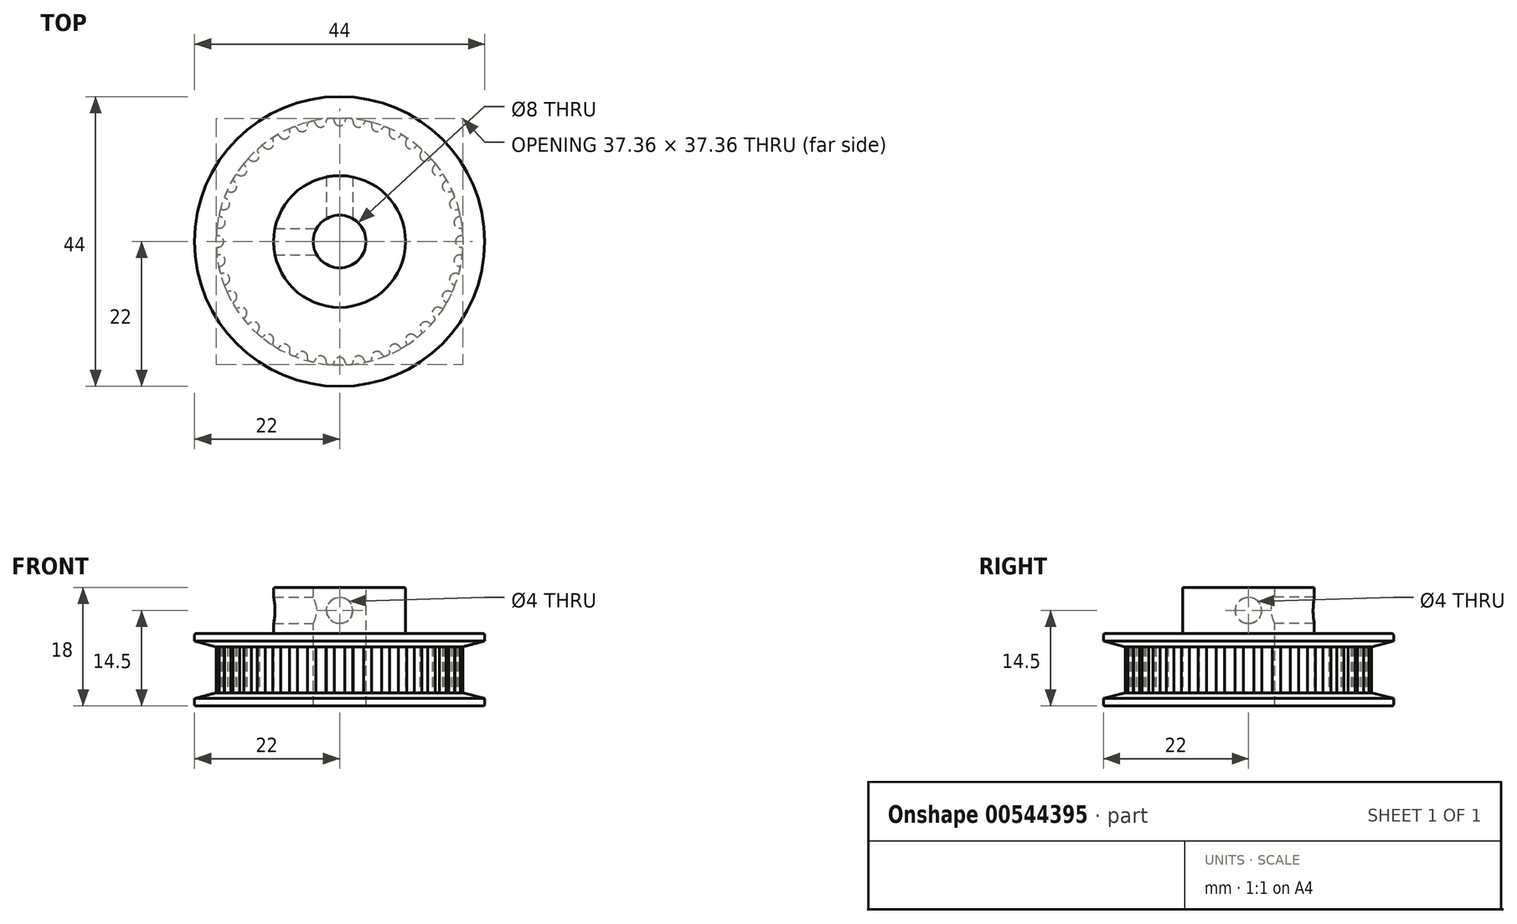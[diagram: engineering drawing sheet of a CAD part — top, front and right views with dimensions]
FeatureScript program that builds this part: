
annotation { "Feature Type Name" : "Feature", "Feature Type Description" : "" }
export const myFeature = defineFeature(function(context is Context, id is Id, definition is map)
    precondition{}
    {
        {
            assignVariable(context, id + "F0", {"name" : "teeth", "anyValue" : 40});
        }
        {
            assignVariable(context, id + "F1", {"name" : "width", "anyValue" : 7});
        }
        {
            var Q0;
            Q0=qCreatedBy(makeId("Top.planeOp"),FACE);
            var sketch = newSketch(context, id + "F2", { "sketchPlane" : qUnion([Q0])});
            skLineSegment(sketch, "E0", {"start": v(0, 0) * mm, "end": v(0, 17.58) * mm, "construction": true});
            skArc(sketch, "E1", {"start": v(1.78, 18.63) * mm, "mid": v(0.15, 18.72) * mm, "end": v(-1.47, 18.66) * mm, "construction": true});
            skArc(sketch, "E2", {"start": v(0, 17.58) * mm, "mid": v(0.49, 17.73) * mm, "end": v(0.8, 18.13) * mm});
            skLineSegment(sketch, "E3", {"start": v(0, 17.58) * mm, "end": v(0, 18.72) * mm, "construction": true});
            skLineSegment(sketch, "E4", {"start": v(0, 18.72) * mm, "end": v(0, 19.1) * mm, "construction": true});
            skArc(sketch, "E5", {"start": v(1.5, 19.04) * mm, "mid": v(0, 19.1) * mm, "end": v(-1.5, 19.04) * mm, "construction": true});
            skLineSegment(sketch, "E6", {"start": v(1.47, 18.66) * mm, "end": v(0, 0) * mm});
            skLineSegment(sketch, "E7", {"start": v(0, 0) * mm, "end": v(-1.47, 18.66) * mm});
            skArc(sketch, "E8", {"start": v(1.15, 18.68) * mm, "mid": v(0.98, 18.63) * mm, "end": v(0.9, 18.47) * mm});
            skArc(sketch, "E9", {"start": v(0.8, 18.13) * mm, "mid": v(0.85, 18.3) * mm, "end": v(0.9, 18.47) * mm});
            skArc(sketch, "E10.MirrorCS", {"start": v(0, 17.58) * mm, "mid": v(-0.49, 17.73) * mm, "end": v(-0.8, 18.13) * mm});
            skArc(sketch, "E11.MirrorCS", {"start": v(-0.8, 18.13) * mm, "mid": v(-0.85, 18.3) * mm, "end": v(-0.9, 18.47) * mm});
            skArc(sketch, "E12.MirrorCS", {"start": v(-1.15, 18.68) * mm, "mid": v(-0.98, 18.63) * mm, "end": v(-0.9, 18.47) * mm});
            skArc(sketch, "E13", {"start": v(0, 18.72) * mm, "mid": v(-0.3, 18.72) * mm, "end": v(-0.6, 18.7) * mm, "construction": true});
            skArc(sketch, "E14", {"start": v(1.39, 17.52) * mm, "mid": v(0, 17.58) * mm, "end": v(-1.39, 17.52) * mm, "construction": true});
            skArc(sketch, "E15", {"start": v(-1.15, 18.68) * mm, "mid": v(-1.31, 18.67) * mm, "end": v(-1.47, 18.66) * mm});
            skArc(sketch, "E16", {"start": v(1.15, 18.68) * mm, "mid": v(1.31, 18.67) * mm, "end": v(1.47, 18.66) * mm});
            skSolve(sketch);
        }
        {
            var Q0;
            Q0=makeQuery(id+"F2.imprint","IMPRINT",FACE,{"disambiguationData":[TD([[makeQuery(id+"F2.imprint","IMPRINT",EDGE,{"derivedFrom":sQuery(id+"F2.wireOp",EDGE,"E2")}),-1.0]])]});
            var Q1;
            {var subQ1=sQuery(id+"F2.wireOp",EDGE,"N9a9pOVT-NxnP-9PMo-Yz0L-ytRW1WlfzG62");Q1=makeQuery(id+"F2.imprint","IMPRINT",FACE,{"disambiguationData":[TD([[makeQuery(id+"F2.imprint","IMPRINT",EDGE,{"derivedFrom":subQ1}),-1.0]])]});}
            var Q2;
            {var subQ0=sQuery(id+"F2.wireOp",EDGE,"E6");Q2=makeQuery(id+"F2.imprint","IMPRINT",FACE,{"disambiguationData":[TD([[makeQuery(id+"F2.imprint","IMPRINT",EDGE,{"derivedFrom":subQ0}),-1.0]])]});}
            extrude(context, id + "F3", {"entities" : qUnion([Q0, Q1, Q2]), "depth" : (getVariable(context, 'width')) * mm, "offsetDistance" : 25 * mm, "symmetric" : true});
        }
        {
            var Q0;
            Q0=makeQuery(id+"F3.opExtrude","SWEPT_BODY",BODY,{"disambiguationData":[OSD([sQuery(id+"F2.wireOp",EDGE,"E1"),sQuery(id+"F2.wireOp",EDGE,"E2"),sQuery(id+"F2.wireOp",EDGE,"WtW3y5By-gfdo-wMA2-XeKf-OYMCoWhlFWBV"),sQuery(id+"F2.wireOp",EDGE,"E6"),sQuery(id+"F2.wireOp",EDGE,"E7"),sQuery(id+"F2.wireOp",EDGE,"N9a9pOVT-NxnP-9PMo-Yz0L-ytRW1WlfzG62"),sQuery(id+"F2.wireOp",EDGE,"E8"),sQuery(id+"F2.wireOp",EDGE,"E9"),sQuery(id+"F2.wireOp",EDGE,"E10.MirrorCS"),sQuery(id+"F2.wireOp",EDGE,"E11.MirrorCS"),sQuery(id+"F2.wireOp",EDGE,"E12.MirrorCS")])]});
            var Q1;
            Q1=makeQuery(id+"F3.opExtrude","SWEPT_EDGE",EDGE,{"disambiguationData":[OSD([sQuery(id+"F2.wireOp",EDGE,"E6"),sQuery(id+"F2.wireOp",EDGE,"E7")])]});
            circularPattern(context, id + "F4", {"operationType" : NewBodyOperationType.ADD, "entities" : qUnion([Q0]), "axis" : qUnion([Q1]), "angle" : 360 * degree, "instanceCount" : getVariable(context, 'teeth'), "equalSpace" : true});
        }
        {
            var Q0;
            {var subQ0=makeQuery(id+"F3.opExtrude","CAP_FACE",FACE,{"disambiguationData":[OSD([sQuery(id+"F2.wireOp",EDGE,"E2"),sQuery(id+"F2.wireOp",EDGE,"E6"),sQuery(id+"F2.wireOp",EDGE,"E7"),sQuery(id+"F2.wireOp",EDGE,"E8"),sQuery(id+"F2.wireOp",EDGE,"E9"),sQuery(id+"F2.wireOp",EDGE,"E10.MirrorCS"),sQuery(id+"F2.wireOp",EDGE,"E11.MirrorCS"),sQuery(id+"F2.wireOp",EDGE,"E12.MirrorCS"),sQuery(id+"F2.wireOp",EDGE,"E15"),sQuery(id+"F2.wireOp",EDGE,"E16")])],"isStart":true});Q0=makeQuery(id+"F4.boolean.opBoolean","MERGE",FACE,{"derivedFrom":[subQ0,makeQuery(id+"F4.opPattern","COPY",FACE,{"derivedFrom":subQ0,"instanceName":"1"}),makeQuery(id+"F4.opPattern","COPY",FACE,{"derivedFrom":subQ0,"instanceName":"2"}),makeQuery(id+"F4.opPattern","COPY",FACE,{"derivedFrom":subQ0,"instanceName":"3"}),makeQuery(id+"F4.opPattern","COPY",FACE,{"derivedFrom":subQ0,"instanceName":"4"}),makeQuery(id+"F4.opPattern","COPY",FACE,{"derivedFrom":subQ0,"instanceName":"5"}),makeQuery(id+"F4.opPattern","COPY",FACE,{"derivedFrom":subQ0,"instanceName":"6"}),makeQuery(id+"F4.opPattern","COPY",FACE,{"derivedFrom":subQ0,"instanceName":"7"}),makeQuery(id+"F4.opPattern","COPY",FACE,{"derivedFrom":subQ0,"instanceName":"8"}),makeQuery(id+"F4.opPattern","COPY",FACE,{"derivedFrom":subQ0,"instanceName":"9"}),makeQuery(id+"F4.opPattern","COPY",FACE,{"derivedFrom":subQ0,"instanceName":"10"}),makeQuery(id+"F4.opPattern","COPY",FACE,{"derivedFrom":subQ0,"instanceName":"11"}),makeQuery(id+"F4.opPattern","COPY",FACE,{"derivedFrom":subQ0,"instanceName":"12"}),makeQuery(id+"F4.opPattern","COPY",FACE,{"derivedFrom":subQ0,"instanceName":"13"}),makeQuery(id+"F4.opPattern","COPY",FACE,{"derivedFrom":subQ0,"instanceName":"14"}),makeQuery(id+"F4.opPattern","COPY",FACE,{"derivedFrom":subQ0,"instanceName":"15"}),makeQuery(id+"F4.opPattern","COPY",FACE,{"derivedFrom":subQ0,"instanceName":"16"}),makeQuery(id+"F4.opPattern","COPY",FACE,{"derivedFrom":subQ0,"instanceName":"17"}),makeQuery(id+"F4.opPattern","COPY",FACE,{"derivedFrom":subQ0,"instanceName":"18"}),makeQuery(id+"F4.opPattern","COPY",FACE,{"derivedFrom":subQ0,"instanceName":"19"}),makeQuery(id+"F4.opPattern","COPY",FACE,{"derivedFrom":subQ0,"instanceName":"20"}),makeQuery(id+"F4.opPattern","COPY",FACE,{"derivedFrom":subQ0,"instanceName":"21"}),makeQuery(id+"F4.opPattern","COPY",FACE,{"derivedFrom":subQ0,"instanceName":"22"}),makeQuery(id+"F4.opPattern","COPY",FACE,{"derivedFrom":subQ0,"instanceName":"23"}),makeQuery(id+"F4.opPattern","COPY",FACE,{"derivedFrom":subQ0,"instanceName":"24"}),makeQuery(id+"F4.opPattern","COPY",FACE,{"derivedFrom":subQ0,"instanceName":"25"}),makeQuery(id+"F4.opPattern","COPY",FACE,{"derivedFrom":subQ0,"instanceName":"26"}),makeQuery(id+"F4.opPattern","COPY",FACE,{"derivedFrom":subQ0,"instanceName":"27"}),makeQuery(id+"F4.opPattern","COPY",FACE,{"derivedFrom":subQ0,"instanceName":"28"}),makeQuery(id+"F4.opPattern","COPY",FACE,{"derivedFrom":subQ0,"instanceName":"29"}),makeQuery(id+"F4.opPattern","COPY",FACE,{"derivedFrom":subQ0,"instanceName":"30"}),makeQuery(id+"F4.opPattern","COPY",FACE,{"derivedFrom":subQ0,"instanceName":"31"}),makeQuery(id+"F4.opPattern","COPY",FACE,{"derivedFrom":subQ0,"instanceName":"32"}),makeQuery(id+"F4.opPattern","COPY",FACE,{"derivedFrom":subQ0,"instanceName":"33"}),makeQuery(id+"F4.opPattern","COPY",FACE,{"derivedFrom":subQ0,"instanceName":"34"}),makeQuery(id+"F4.opPattern","COPY",FACE,{"derivedFrom":subQ0,"instanceName":"35"}),makeQuery(id+"F4.opPattern","COPY",FACE,{"derivedFrom":subQ0,"instanceName":"36"}),makeQuery(id+"F4.opPattern","COPY",FACE,{"derivedFrom":subQ0,"instanceName":"37"}),makeQuery(id+"F4.opPattern","COPY",FACE,{"derivedFrom":subQ0,"instanceName":"38"}),makeQuery(id+"F4.opPattern","COPY",FACE,{"derivedFrom":subQ0,"instanceName":"39"})]});}
            var sketch = newSketch(context, id + "F5", { "sketchPlane" : qUnion([Q0])});
            skCircle(sketch, "E17", {"center": v(0, 0) * mm, "radius": 22 * mm});
            skSolve(sketch);
        }
        {
            var Q0;
            Q0=qSketchRegion(id+"F5",true);
            extrude(context, id + "F6", {"entities" : qUnion([Q0]), "operationType" : NewBodyOperationType.ADD, "depth" : 2 * mm, "offsetDistance" : 25 * mm});
        }
        {
            var Q0;
            {var subQ0=makeQuery(id+"F3.opExtrude","CAP_FACE",FACE,{"disambiguationData":[OSD([sQuery(id+"F2.wireOp",EDGE,"E2"),sQuery(id+"F2.wireOp",EDGE,"E6"),sQuery(id+"F2.wireOp",EDGE,"E7"),sQuery(id+"F2.wireOp",EDGE,"E8"),sQuery(id+"F2.wireOp",EDGE,"E9"),sQuery(id+"F2.wireOp",EDGE,"E10.MirrorCS"),sQuery(id+"F2.wireOp",EDGE,"E11.MirrorCS"),sQuery(id+"F2.wireOp",EDGE,"E12.MirrorCS"),sQuery(id+"F2.wireOp",EDGE,"E15"),sQuery(id+"F2.wireOp",EDGE,"E16")])],"isStart":false});Q0=makeQuery(id+"F4.boolean.opBoolean","MERGE",FACE,{"derivedFrom":[subQ0,makeQuery(id+"F4.opPattern","COPY",FACE,{"derivedFrom":subQ0,"instanceName":"1"}),makeQuery(id+"F4.opPattern","COPY",FACE,{"derivedFrom":subQ0,"instanceName":"2"}),makeQuery(id+"F4.opPattern","COPY",FACE,{"derivedFrom":subQ0,"instanceName":"3"}),makeQuery(id+"F4.opPattern","COPY",FACE,{"derivedFrom":subQ0,"instanceName":"4"}),makeQuery(id+"F4.opPattern","COPY",FACE,{"derivedFrom":subQ0,"instanceName":"5"}),makeQuery(id+"F4.opPattern","COPY",FACE,{"derivedFrom":subQ0,"instanceName":"6"}),makeQuery(id+"F4.opPattern","COPY",FACE,{"derivedFrom":subQ0,"instanceName":"7"}),makeQuery(id+"F4.opPattern","COPY",FACE,{"derivedFrom":subQ0,"instanceName":"8"}),makeQuery(id+"F4.opPattern","COPY",FACE,{"derivedFrom":subQ0,"instanceName":"9"}),makeQuery(id+"F4.opPattern","COPY",FACE,{"derivedFrom":subQ0,"instanceName":"10"}),makeQuery(id+"F4.opPattern","COPY",FACE,{"derivedFrom":subQ0,"instanceName":"11"}),makeQuery(id+"F4.opPattern","COPY",FACE,{"derivedFrom":subQ0,"instanceName":"12"}),makeQuery(id+"F4.opPattern","COPY",FACE,{"derivedFrom":subQ0,"instanceName":"13"}),makeQuery(id+"F4.opPattern","COPY",FACE,{"derivedFrom":subQ0,"instanceName":"14"}),makeQuery(id+"F4.opPattern","COPY",FACE,{"derivedFrom":subQ0,"instanceName":"15"}),makeQuery(id+"F4.opPattern","COPY",FACE,{"derivedFrom":subQ0,"instanceName":"16"}),makeQuery(id+"F4.opPattern","COPY",FACE,{"derivedFrom":subQ0,"instanceName":"17"}),makeQuery(id+"F4.opPattern","COPY",FACE,{"derivedFrom":subQ0,"instanceName":"18"}),makeQuery(id+"F4.opPattern","COPY",FACE,{"derivedFrom":subQ0,"instanceName":"19"}),makeQuery(id+"F4.opPattern","COPY",FACE,{"derivedFrom":subQ0,"instanceName":"20"}),makeQuery(id+"F4.opPattern","COPY",FACE,{"derivedFrom":subQ0,"instanceName":"21"}),makeQuery(id+"F4.opPattern","COPY",FACE,{"derivedFrom":subQ0,"instanceName":"22"}),makeQuery(id+"F4.opPattern","COPY",FACE,{"derivedFrom":subQ0,"instanceName":"23"}),makeQuery(id+"F4.opPattern","COPY",FACE,{"derivedFrom":subQ0,"instanceName":"24"}),makeQuery(id+"F4.opPattern","COPY",FACE,{"derivedFrom":subQ0,"instanceName":"25"}),makeQuery(id+"F4.opPattern","COPY",FACE,{"derivedFrom":subQ0,"instanceName":"26"}),makeQuery(id+"F4.opPattern","COPY",FACE,{"derivedFrom":subQ0,"instanceName":"27"}),makeQuery(id+"F4.opPattern","COPY",FACE,{"derivedFrom":subQ0,"instanceName":"28"}),makeQuery(id+"F4.opPattern","COPY",FACE,{"derivedFrom":subQ0,"instanceName":"29"}),makeQuery(id+"F4.opPattern","COPY",FACE,{"derivedFrom":subQ0,"instanceName":"30"}),makeQuery(id+"F4.opPattern","COPY",FACE,{"derivedFrom":subQ0,"instanceName":"31"}),makeQuery(id+"F4.opPattern","COPY",FACE,{"derivedFrom":subQ0,"instanceName":"32"}),makeQuery(id+"F4.opPattern","COPY",FACE,{"derivedFrom":subQ0,"instanceName":"33"}),makeQuery(id+"F4.opPattern","COPY",FACE,{"derivedFrom":subQ0,"instanceName":"34"}),makeQuery(id+"F4.opPattern","COPY",FACE,{"derivedFrom":subQ0,"instanceName":"35"}),makeQuery(id+"F4.opPattern","COPY",FACE,{"derivedFrom":subQ0,"instanceName":"36"}),makeQuery(id+"F4.opPattern","COPY",FACE,{"derivedFrom":subQ0,"instanceName":"37"}),makeQuery(id+"F4.opPattern","COPY",FACE,{"derivedFrom":subQ0,"instanceName":"38"}),makeQuery(id+"F4.opPattern","COPY",FACE,{"derivedFrom":subQ0,"instanceName":"39"})]});}
            var sketch = newSketch(context, id + "F7", { "sketchPlane" : qUnion([Q0])});
            skCircle(sketch, "E18", {"center": v(0, 0) * mm, "radius": 22 * mm});
            skSolve(sketch);
        }
        {
            var Q0;
            Q0=qSketchRegion(id+"F7",true);
            extrude(context, id + "F8", {"entities" : qUnion([Q0]), "operationType" : NewBodyOperationType.ADD, "depth" : 2 * mm, "offsetDistance" : 25 * mm});
        }
        {
            var Q0;
            Q0=makeQuery(id+"F8.opExtrude","CAP_FACE",FACE,{"disambiguationData":[OSD([sQuery(id+"F7.wireOp",EDGE,"E18")])],"isStart":false});
            var sketch = newSketch(context, id + "F9", { "sketchPlane" : qUnion([Q0])});
            skCircle(sketch, "E19", {"center": v(0, 0) * mm, "radius": 10 * mm});
            skSolve(sketch);
        }
        {
            var Q0;
            Q0=qSketchRegion(id+"F9",true);
            extrude(context, id + "F10", {"entities" : qUnion([Q0]), "operationType" : NewBodyOperationType.ADD, "depth" : 7 * mm, "offsetDistance" : 25 * mm});
        }
        {
            var Q0;
            Q0=makeQuery(id+"F10.opExtrude","CAP_FACE",FACE,{"disambiguationData":[OSD([sQuery(id+"F9.wireOp",EDGE,"E19")])],"isStart":false});
            var sketch = newSketch(context, id + "F11", { "sketchPlane" : qUnion([Q0])});
            skCircle(sketch, "E20", {"center": v(0, 0) * mm, "radius": 4 * mm});
            skSolve(sketch);
        }
        {
            var Q0;
            Q0=qSketchRegion(id+"F11",true);
            extrude(context, id + "F12", {"entities" : qUnion([Q0]), "operationType" : NewBodyOperationType.REMOVE, "endBound" : BoundingType.THROUGH_ALL, "oppositeDirection" : true, "depth" : 25 * mm, "offsetDistance" : 25 * mm});
        }
        {
            var Q0;
            Q0=qCreatedBy(makeId("Front.planeOp"),FACE);
            var sketch = newSketch(context, id + "F13", { "sketchPlane" : qUnion([Q0])});
            skCircle(sketch, "E21", {"center": v(0, 9) * mm, "radius": 2 * mm});
            skSolve(sketch);
        }
        {
            var Q0;
            Q0=qSketchRegion(id+"F13",true);
            extrude(context, id + "F14", {"entities" : qUnion([Q0]), "operationType" : NewBodyOperationType.REMOVE, "endBound" : BoundingType.THROUGH_ALL, "oppositeDirection" : true, "depth" : 25 * mm, "offsetDistance" : 25 * mm});
        }
        {
            var Q0;
            Q0=qCreatedBy(makeId("Right.planeOp"),FACE);
            var sketch = newSketch(context, id + "F15", { "sketchPlane" : qUnion([Q0])});
            skCircle(sketch, "E22", {"center": v(0, 9) * mm, "radius": 2 * mm});
            skSolve(sketch);
        }
        {
            var Q0;
            Q0=qSketchRegion(id+"F15",true);
            extrude(context, id + "F16", {"entities" : qUnion([Q0]), "operationType" : NewBodyOperationType.REMOVE, "endBound" : BoundingType.THROUGH_ALL, "oppositeDirection" : true, "depth" : 25 * mm, "offsetDistance" : 25 * mm});
        }
        {
            var Q0;
            Q0=makeQuery(id+"F6.opExtrude","CAP_EDGE",EDGE,{"disambiguationData":[OSD([sQuery(id+"F5.wireOp",EDGE,"E17")])],"isStart":true});
            var Q1;
            Q1=makeQuery(id+"F8.opExtrude","CAP_EDGE",EDGE,{"disambiguationData":[OSD([sQuery(id+"F7.wireOp",EDGE,"E18")])],"isStart":true});
            chamfer(context, id + "F17", {"entities" : qUnion([Q0, Q1]), "chamferType" : ChamferType.OFFSET_ANGLE, "width" : 3.25 * mm, "oppositeDirection" : true, "angle" : 15 * degree, "tangentPropagation" : true});
        }
        {
            var Q0;
            Q0=makeQuery(id+"F10.opExtrude","CAP_EDGE",EDGE,{"disambiguationData":[OSD([sQuery(id+"F9.wireOp",EDGE,"E19")])],"isStart":true});
            var Q1;
            Q1=makeQuery(id+"F10.opExtrude","CAP_EDGE",EDGE,{"disambiguationData":[OSD([sQuery(id+"F9.wireOp",EDGE,"E19")])],"isStart":false});
            var Q2;
            Q2=makeQuery(id+"F8.opExtrude","CAP_EDGE",EDGE,{"disambiguationData":[OSD([sQuery(id+"F7.wireOp",EDGE,"E18")])],"isStart":false});
            var Q3;
            Q3=makeQuery(id+"F6.opExtrude","CAP_EDGE",EDGE,{"disambiguationData":[OSD([sQuery(id+"F5.wireOp",EDGE,"E17")])],"isStart":false});
            fillet(context, id + "F18", {"entities" : qUnion([Q0, Q1, Q2, Q3]), "radius" : 0.25 * mm, "tangentPropagation" : true, "allowEdgeOverflow" : false});
        }
    });
